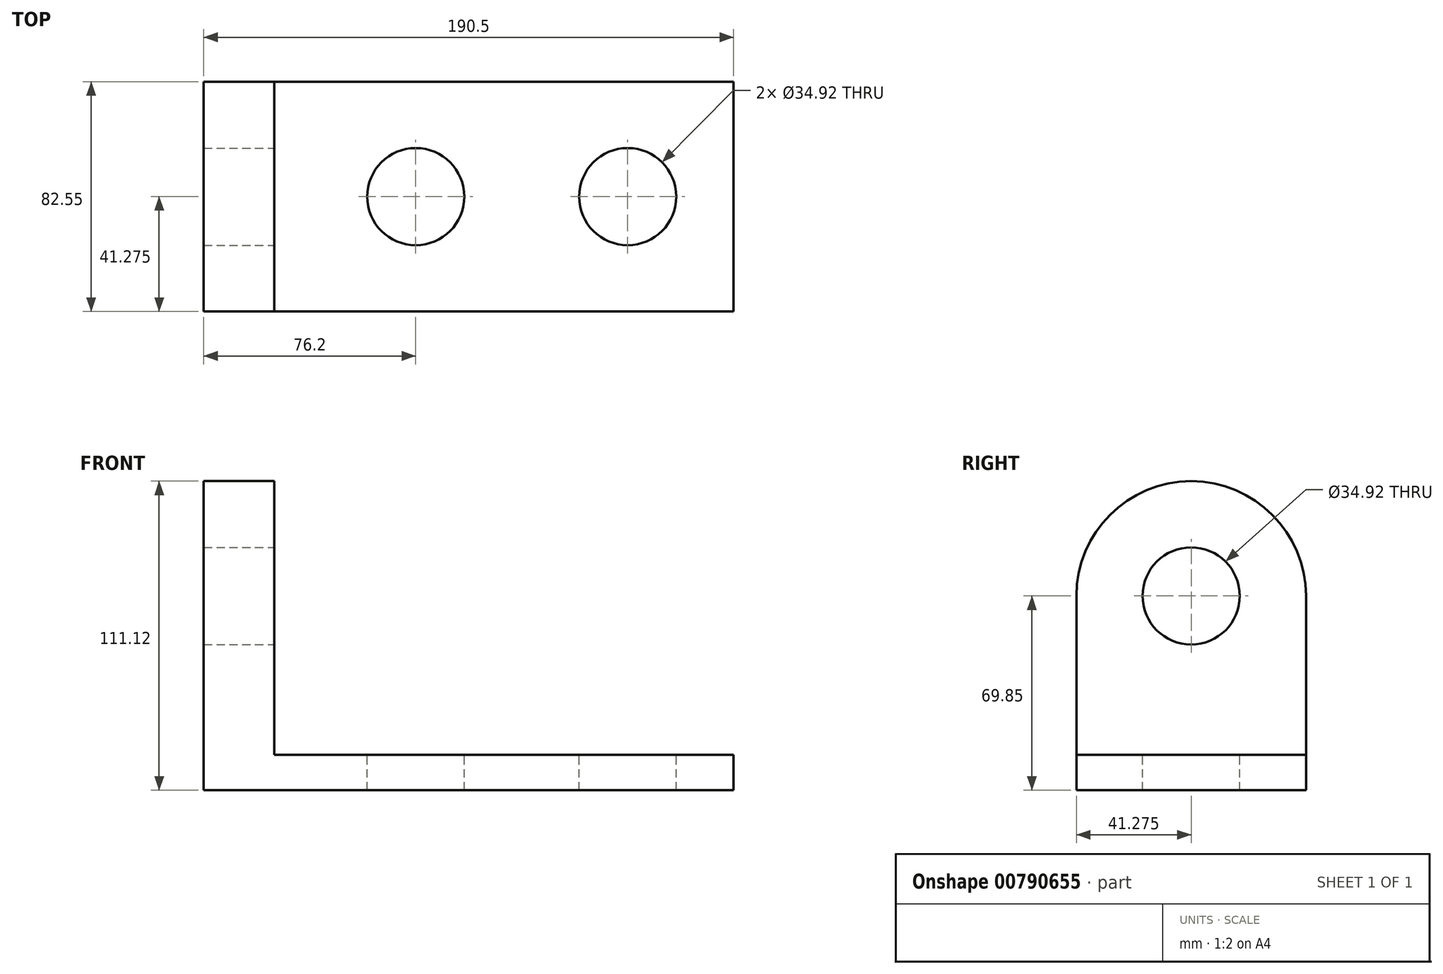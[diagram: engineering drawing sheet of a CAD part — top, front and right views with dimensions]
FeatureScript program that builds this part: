
annotation { "Feature Type Name" : "Feature", "Feature Type Description" : "" }
export const myFeature = defineFeature(function(context is Context, id is Id, definition is map)
    precondition{}
    {
        {
            var Q0;
            Q0=qCreatedBy(makeId("Front.planeOp"),FACE);
            var sketch = newSketch(context, id + "F0", { "sketchPlane" : qUnion([Q0])});
            skLineSegment(sketch, "E0", {"start": v(0, 0) * mm, "end": v(0, 127) * mm});
            skLineSegment(sketch, "E1", {"start": v(0, 127) * mm, "end": v(25.4, 127) * mm});
            skLineSegment(sketch, "E2", {"start": v(0, 0) * mm, "end": v(190.5, 0) * mm});
            skLineSegment(sketch, "E3", {"start": v(190.5, 0) * mm, "end": v(190.5, 12.7) * mm});
            skLineSegment(sketch, "E4", {"start": v(190.5, 12.7) * mm, "end": v(25.4, 12.7) * mm});
            skLineSegment(sketch, "E5", {"start": v(25.4, 12.7) * mm, "end": v(25.4, 127) * mm});
            skSolve(sketch);
        }
        {
            var Q0;
            Q0 = qSketchRegion(id + "F0", true);
            extrude(context, id + "F1", {"entities" : qUnion([Q0]), "depth" : 82.55 * mm, "offsetDistance" : 25.4 * mm});
        }
        {
            var Q0;
            Q0=makeQuery(id+"F1.opExtrude","SWEPT_FACE",FACE,{"disambiguationData":[OSD([sQuery(id+"F0.wireOp",EDGE,"E5")])]});
            var sketch = newSketch(context, id + "F2", { "sketchPlane" : qUnion([Q0])});
            skLineSegment(sketch, "E6", {"start": v(-82.55, 12.7) * mm, "end": v(-82.55, 69.85) * mm, "construction": true});
            skLineSegment(sketch, "E7", {"start": v(-82.55, 69.85) * mm, "end": v(0, 69.85) * mm, "construction": true});
            skLineSegment(sketch, "E8", {"start": v(0, 69.85) * mm, "end": v(0, 12.7) * mm, "construction": true});
            skLineSegment(sketch, "E9", {"start": v(-41.28, 69.85) * mm, "end": v(-41.28, 12.7) * mm, "construction": true});
            skArc(sketch, "E10", {"start": v(0, 69.85) * mm, "mid": v(-41.28, 111.12) * mm, "end": v(-82.55, 69.85) * mm});
            skCircle(sketch, "E11", {"center": v(-41.28, 69.85) * mm, "radius": 17.46 * mm});
            skSolve(sketch);
        }
        {
            var Q0;
            Q0 = qSketchRegion(id + "F2", true);
            var Q1;
            {var subQ0=sQuery(id+"F2.wireOp",EDGE,"E10");Q1=makeQuery(id+"F2.imprint","IMPRINT",FACE,{"disambiguationData":[TD([[makeQuery(id+"F2.imprint","IMPRINT",EDGE,{"derivedFrom":subQ0}),-1.0]])]});}
            extrude(context, id + "F3", {"entities" : qUnion([Q0, Q1]), "operationType" : NewBodyOperationType.REMOVE, "endBound" : BoundingType.THROUGH_ALL, "oppositeDirection" : true, "depth" : 25.4 * mm, "offsetDistance" : 25.4 * mm});
        }
        {
            var Q0;
            Q0=makeQuery(id+"F1.opExtrude","SWEPT_FACE",FACE,{"disambiguationData":[OSD([sQuery(id+"F0.wireOp",EDGE,"E4")])]});
            var sketch = newSketch(context, id + "F4", { "sketchPlane" : qUnion([Q0])});
            skLineSegment(sketch, "E12", {"start": v(190.5, -41.28) * mm, "end": v(152.4, -41.28) * mm, "construction": true});
            skCircle(sketch, "E13", {"center": v(152.4, -41.28) * mm, "radius": 17.46 * mm});
            skLineSegment(sketch, "E14", {"start": v(152.4, -41.28) * mm, "end": v(76.2, -41.28) * mm, "construction": true});
            skCircle(sketch, "E15", {"center": v(76.2, -41.28) * mm, "radius": 17.46 * mm});
            skSolve(sketch);
        }
        {
            var Q0;
            Q0 = qSketchRegion(id + "F4", true);
            var Q1;
            Q1=makeQuery(id+"F4.imprint","IMPRINT",FACE,{"disambiguationData":[TD([[makeQuery(id+"F4.imprint","IMPRINT",EDGE,{"derivedFrom":sQuery(id+"F4.wireOp",EDGE,"E15")}),1.0]])]});
            extrude(context, id + "F5", {"entities" : qUnion([Q0, Q1]), "operationType" : NewBodyOperationType.REMOVE, "endBound" : BoundingType.THROUGH_ALL, "oppositeDirection" : true, "depth" : 25.4 * mm, "offsetDistance" : 25.4 * mm});
        }
    });
